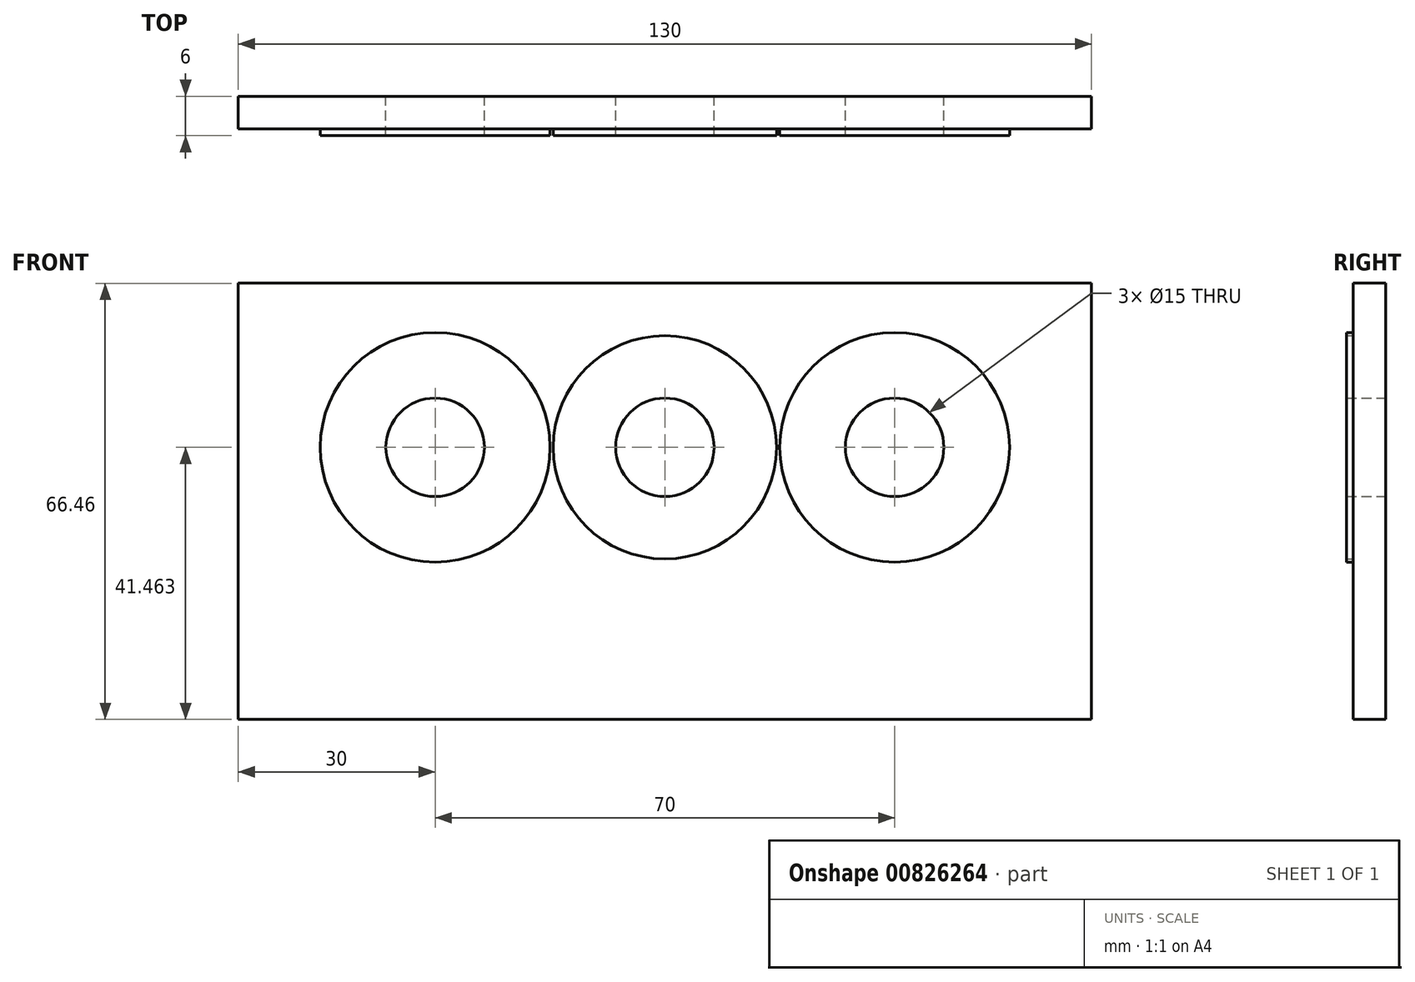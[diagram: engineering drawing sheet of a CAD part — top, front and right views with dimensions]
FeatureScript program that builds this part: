
annotation { "Feature Type Name" : "Feature", "Feature Type Description" : "" }
export const myFeature = defineFeature(function(context is Context, id is Id, definition is map)
    precondition{}
    {
        {
            var Q0;
            Q0=qCreatedBy(makeId("Front.planeOp"),FACE);
            var sketch = newSketch(context, id + "F0", { "sketchPlane" : qUnion([Q0])});
            skLineSegment(sketch, "E0", {"start": v(-65, 33.23) * mm, "end": v(65, 33.23) * mm});
            skLineSegment(sketch, "E1", {"start": v(65, 33.23) * mm, "end": v(65, -33.23) * mm});
            skLineSegment(sketch, "E2", {"start": v(65, -33.23) * mm, "end": v(-65, -33.23) * mm});
            skLineSegment(sketch, "E3", {"start": v(-65, -33.23) * mm, "end": v(-65, 33.23) * mm});
            skLineSegment(sketch, "E4", {"start": v(0, 0) * mm, "end": v(0, 33.23) * mm, "construction": true});
            skLineSegment(sketch, "E5", {"start": v(0, 0) * mm, "end": v(-65, 0) * mm, "construction": true});
            skCircle(sketch, "E6", {"center": v(35, 8.23) * mm, "radius": 17.5 * mm});
            skCircle(sketch, "E7", {"center": v(-35, 8.23) * mm, "radius": 17.5 * mm});
            skLineSegment(sketch, "E8", {"start": v(-35, 8.23) * mm, "end": v(-35, 33.23) * mm, "construction": true});
            skLineSegment(sketch, "E9", {"start": v(-35, 8.23) * mm, "end": v(-65, 8.23) * mm, "construction": true});
            skLineSegment(sketch, "E10", {"start": v(65, 8.23) * mm, "end": v(35, 8.23) * mm, "construction": true});
            skLineSegment(sketch, "E11", {"start": v(35, 8.23) * mm, "end": v(35, 33.23) * mm, "construction": true});
            skCircle(sketch, "E12", {"center": v(0, 8.23) * mm, "radius": 17.5 * mm});
            skLineSegment(sketch, "E13", {"start": v(-35, 8.23) * mm, "end": v(0, 8.23) * mm, "construction": true});
            skLineSegment(sketch, "E14", {"start": v(35, 8.23) * mm, "end": v(0, 8.23) * mm, "construction": true});
            skCircle(sketch, "E15", {"center": v(0, 8.23) * mm, "radius": 5 * mm});
            skCircle(sketch, "E16", {"center": v(-35, 8.23) * mm, "radius": 7.5 * mm});
            skCircle(sketch, "E17", {"center": v(0, 8.23) * mm, "radius": 7.5 * mm});
            skCircle(sketch, "E18", {"center": v(35, 8.23) * mm, "radius": 7.5 * mm});
            skCircle(sketch, "E19", {"center": v(0, 8.23) * mm, "radius": 17 * mm});
            skSolve(sketch);
        }
        {
            var Q0;
            Q0=makeQuery(id+"F0.imprint","IMPRINT",FACE,{"disambiguationData":[TD([[makeQuery(id+"F0.imprint","IMPRINT",EDGE,{"derivedFrom":sQuery(id+"F0.wireOp",EDGE,"E0")}),-1.0]])]});
            var Q1;
            Q1=makeQuery(id+"F0.imprint","IMPRINT",FACE,{"disambiguationData":[TD([[makeQuery(id+"F0.imprint","IMPRINT",EDGE,{"derivedFrom":sQuery(id+"F0.wireOp",EDGE,"E7")}),1.0]])]});
            var Q2;
            {var subQ0=sQuery(id+"F0.wireOp",EDGE,"E12");var subQ1=makeQuery(id+"F0.imprint","INTERSECT",VERTEX,{"derivedFrom":[sQuery(id+"F0.wireOp",EDGE,"E6"),subQ0]});Q2=makeQuery(id+"F0.imprint","IMPRINT",FACE,{"disambiguationData":[TD([[makeQuery(id+"F0.imprint","IMPRINT",EDGE,{"disambiguationData":[TD([[subQ1,-1.0]])],"derivedFrom":subQ0}),1.0]])]});}
            var Q3;
            Q3=makeQuery(id+"F0.imprint","IMPRINT",FACE,{"disambiguationData":[TD([[makeQuery(id+"F0.imprint","IMPRINT",EDGE,{"derivedFrom":sQuery(id+"F0.wireOp",EDGE,"E6")}),1.0]])]});
            var Q4;
            Q4=makeQuery(id+"F0.imprint","IMPRINT",FACE,{"disambiguationData":[TD([[makeQuery(id+"F0.imprint","IMPRINT",EDGE,{"derivedFrom":sQuery(id+"F0.wireOp",EDGE,"E17")}),-1.0]])]});
            extrude(context, id + "F1", {"entities" : qUnion([Q0, Q1, Q2, Q3, Q4]), "depth" : 5 * mm, "offsetDistance" : 25 * mm});
        }
        {
            var Q0;
            Q0=makeQuery(id+"F0.imprint","IMPRINT",FACE,{"disambiguationData":[TD([[makeQuery(id+"F0.imprint","IMPRINT",EDGE,{"derivedFrom":sQuery(id+"F0.wireOp",EDGE,"E6")}),1.0]])]});
            extrude(context, id + "F2", {"entities" : qUnion([Q0]), "operationType" : NewBodyOperationType.ADD, "depth" : 6 * mm, "offsetDistance" : 25 * mm});
        }
        {
            var Q0;
            Q0=makeQuery(id+"F0.imprint","IMPRINT",FACE,{"disambiguationData":[TD([[makeQuery(id+"F0.imprint","IMPRINT",EDGE,{"derivedFrom":sQuery(id+"F0.wireOp",EDGE,"E7")}),1.0]])]});
            extrude(context, id + "F3", {"entities" : qUnion([Q0]), "operationType" : NewBodyOperationType.ADD, "depth" : 6 * mm, "offsetDistance" : 25 * mm});
        }
        {
            var Q0;
            Q0=makeQuery(id+"F0.imprint","IMPRINT",FACE,{"disambiguationData":[TD([[makeQuery(id+"F0.imprint","IMPRINT",EDGE,{"derivedFrom":sQuery(id+"F0.wireOp",EDGE,"E17")}),-1.0]])]});
            extrude(context, id + "F4", {"entities" : qUnion([Q0]), "operationType" : NewBodyOperationType.ADD, "depth" : 6 * mm, "offsetDistance" : 25 * mm});
        }
    });
